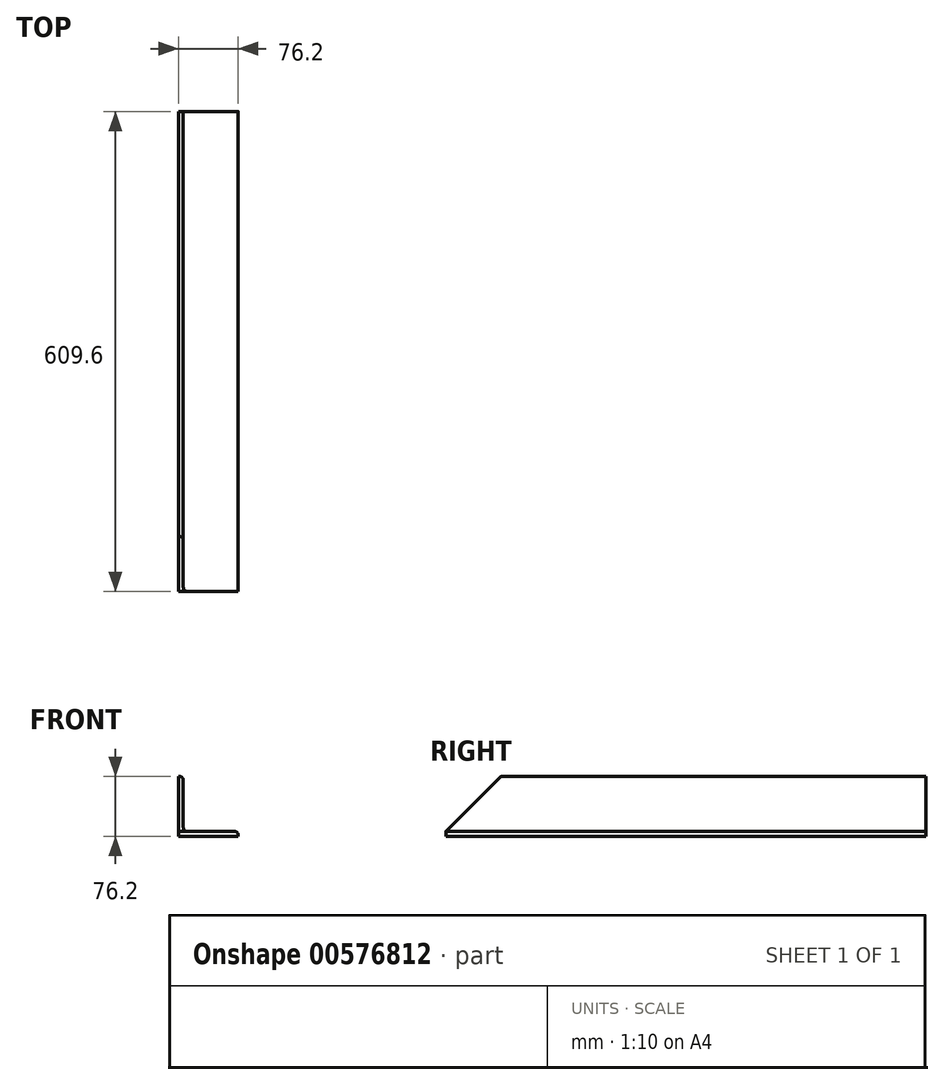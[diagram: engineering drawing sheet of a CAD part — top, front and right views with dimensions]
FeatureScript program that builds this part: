
annotation { "Feature Type Name" : "Feature", "Feature Type Description" : "" }
export const myFeature = defineFeature(function(context is Context, id is Id, definition is map)
    precondition{}
    {
        {
            var Q0;
            Q0=qCreatedBy(makeId("Front.planeOp"),FACE);
            var sketch = newSketch(context, id + "F0", { "sketchPlane" : qUnion([Q0])});
            skLineSegment(sketch, "E0", {"start": v(0, 0) * mm, "end": v(0, 76.2) * mm});
            skLineSegment(sketch, "E1", {"start": v(0, 76.2) * mm, "end": v(6.35, 76.2) * mm});
            skLineSegment(sketch, "E2", {"start": v(6.35, 76.2) * mm, "end": v(6.35, 6.35) * mm});
            skLineSegment(sketch, "E3", {"start": v(6.35, 6.35) * mm, "end": v(76.2, 6.35) * mm});
            skLineSegment(sketch, "E4", {"start": v(76.2, 6.35) * mm, "end": v(76.2, 0) * mm});
            skLineSegment(sketch, "E5", {"start": v(76.2, 0) * mm, "end": v(0, 0) * mm});
            skSolve(sketch);
        }
        {
            var Q0;
            Q0 = qSketchRegion(id + "F0", true);
            extrude(context, id + "F1", {"entities" : qUnion([Q0]), "endBound" : BoundingType.SYMMETRIC, "depth" : 609.6 * mm, "offsetDistance" : 25.4 * mm});
        }
        {
            var Q0;
            Q0=makeQuery(id+"F1.opExtrude","SWEPT_EDGE",EDGE,{"disambiguationData":[OSD([sQuery(id+"F0.wireOp",EDGE,"E2"),sQuery(id+"F0.wireOp",EDGE,"E3")])]});
            var Q1;
            Q1=makeQuery(id+"F1.opExtrude","SWEPT_EDGE",EDGE,{"disambiguationData":[OSD([sQuery(id+"F0.wireOp",EDGE,"E1"),sQuery(id+"F0.wireOp",EDGE,"E2")])]});
            var Q2;
            Q2=makeQuery(id+"F1.opExtrude","SWEPT_EDGE",EDGE,{"disambiguationData":[OSD([sQuery(id+"F0.wireOp",EDGE,"E3"),sQuery(id+"F0.wireOp",EDGE,"E4")])]});
            fillet(context, id + "F2", {"entities" : qUnion([Q0, Q1, Q2]), "radius" : 5.08 * mm, "tangentPropagation" : true, "allowEdgeOverflow" : false});
        }
        {
            var Q0;
            Q0=makeQuery(id+"F1.opExtrude","SWEPT_FACE",FACE,{"disambiguationData":[OSD([sQuery(id+"F0.wireOp",EDGE,"E0")])]});
            var sketch = newSketch(context, id + "F3", { "sketchPlane" : qUnion([Q0])});
            skPoint(sketch, "E6.0", {"position": v(304.8, 6.35) * mm});
            skLineSegment(sketch, "E7", {"start": v(304.8, 6.35) * mm, "end": v(190.89, 120.26) * mm});
            skLineSegment(sketch, "E8", {"start": v(190.89, 120.26) * mm, "end": v(304.8, 120.26) * mm});
            skLineSegment(sketch, "E9", {"start": v(304.8, 120.26) * mm, "end": v(304.8, 6.35) * mm});
            skSolve(sketch);
        }
        {
            var Q0;
            Q0 = qSketchRegion(id + "F3", true);
            extrude(context, id + "F4", {"entities" : qUnion([Q0]), "operationType" : NewBodyOperationType.REMOVE, "oppositeDirection" : true, "depth" : 25.4 * mm, "offsetDistance" : 25.4 * mm});
        }
    });
